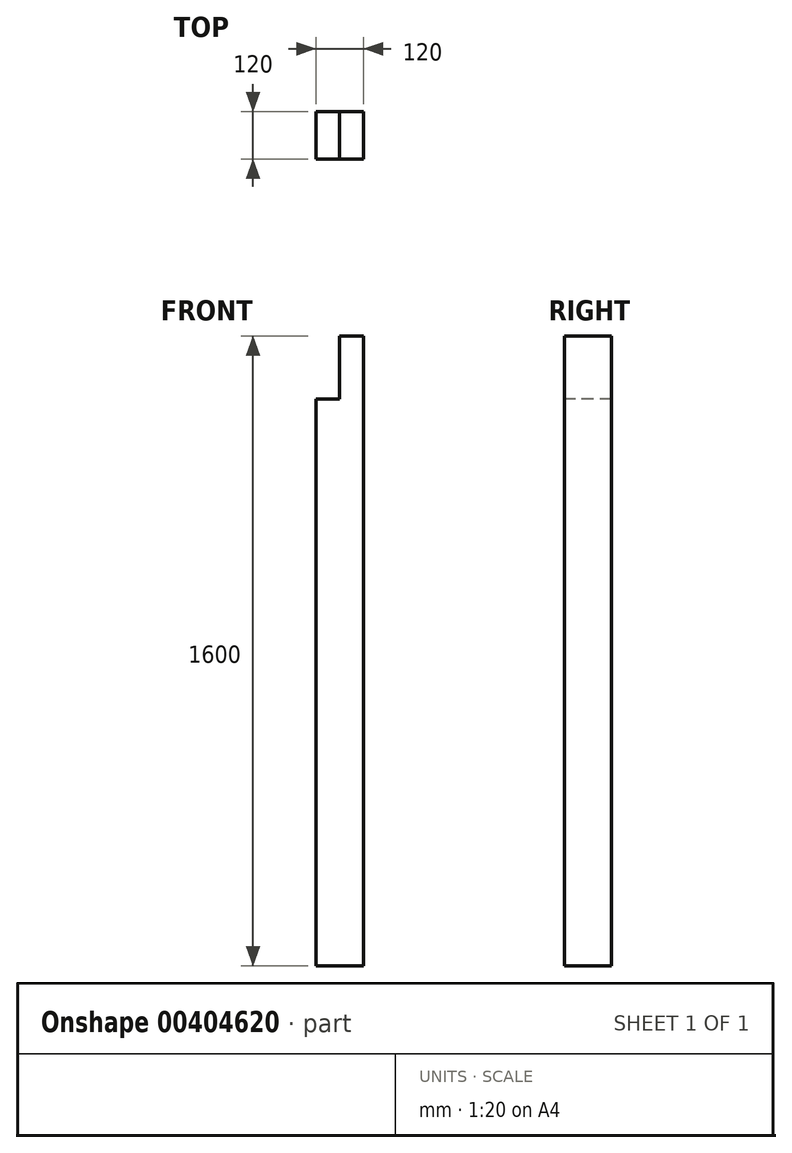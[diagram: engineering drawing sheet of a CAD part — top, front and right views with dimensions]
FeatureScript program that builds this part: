
annotation { "Feature Type Name" : "Feature", "Feature Type Description" : "" }
export const myFeature = defineFeature(function(context is Context, id is Id, definition is map)
    precondition{}
    {
        {
            assignVariable(context, id + "F0", {"name" : "hLounge", "anyValue" : 1600});
        }
        {
            var Q0;
            Q0=qCreatedBy(makeId("Top.planeOp"),FACE);
            var sketch = newSketch(context, id + "F1", { "sketchPlane" : qUnion([Q0])});
            skLineSegment(sketch, "E0.bottom", {"start": v(-60, 60) * mm, "end": v(60, 60) * mm});
            skLineSegment(sketch, "E0.top", {"start": v(-60, -60) * mm, "end": v(60, -60) * mm});
            skLineSegment(sketch, "E0.left", {"start": v(-60, 60) * mm, "end": v(-60, -60) * mm});
            skLineSegment(sketch, "E0.right", {"start": v(60, 60) * mm, "end": v(60, -60) * mm});
            skSolve(sketch);
        }
        {
            var Q0;
            Q0=makeQuery(id+"F1.imprint","IMPRINT",FACE,{"disambiguationData":[TD([[makeQuery(id+"F1.imprint","IMPRINT",EDGE,{"derivedFrom":sQuery(id+"F1.wireOp",EDGE,"E0.bottom")}),-1.0]])]});
            extrude(context, id + "F2", {"entities" : qUnion([Q0]), "depth" : (getVariable(context, 'hLounge')) * mm});
        }
        {
            var Q0;
            Q0=makeQuery(id+"F2.opExtrude","SWEPT_FACE",FACE,{"disambiguationData":[OSD([sQuery(id+"F1.wireOp",EDGE,"E0.top")])]});
            var sketch = newSketch(context, id + "F3", { "sketchPlane" : qUnion([Q0])});
            skLineSegment(sketch, "E1.bottom", {"start": v(-60, 1600) * mm, "end": v(0, 1600) * mm});
            skLineSegment(sketch, "E1.top", {"start": v(-60, 1440) * mm, "end": v(0, 1440) * mm});
            skLineSegment(sketch, "E1.left", {"start": v(-60, 1600) * mm, "end": v(-60, 1440) * mm});
            skLineSegment(sketch, "E1.right", {"start": v(0, 1600) * mm, "end": v(0, 1440) * mm});
            skSolve(sketch);
        }
        {
            var Q0;
            Q0 = qSketchRegion(id + "F3", true);
            extrude(context, id + "F4", {"entities" : qUnion([Q0]), "operationType" : NewBodyOperationType.REMOVE, "endBound" : BoundingType.UP_TO_NEXT, "oppositeDirection" : true, "depth" : 25 * mm});
        }
    });
